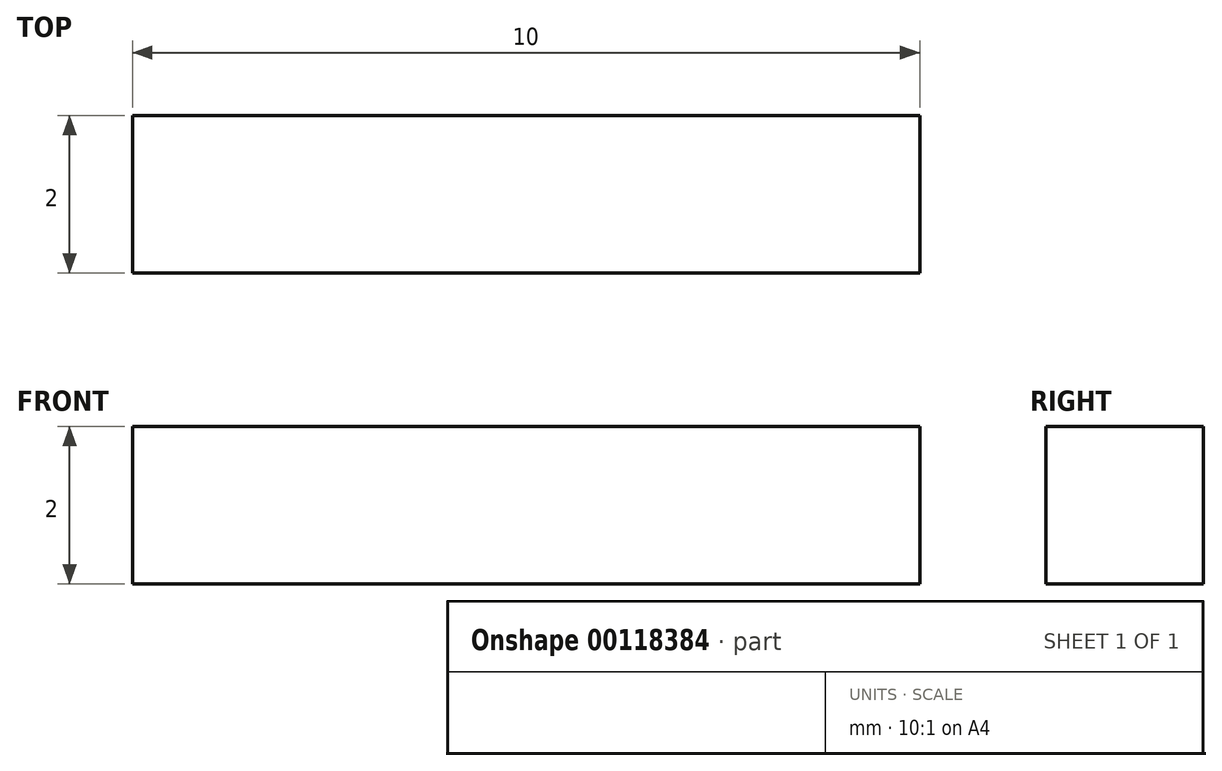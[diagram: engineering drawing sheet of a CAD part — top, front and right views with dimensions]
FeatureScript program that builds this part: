
annotation { "Feature Type Name" : "Feature", "Feature Type Description" : "" }
export const myFeature = defineFeature(function(context is Context, id is Id, definition is map)
    precondition{}
    {
        {
            var Q0;
            Q0=qCreatedBy(makeId("Top.planeOp"),FACE);
            var sketch = newSketch(context, id + "F0", { "sketchPlane" : qUnion([Q0])});
            skLineSegment(sketch, "E0.bottom", {"start": v(5, -1) * mm, "end": v(-5, -1) * mm});
            skLineSegment(sketch, "E0.top", {"start": v(5, 1) * mm, "end": v(-5, 1) * mm});
            skLineSegment(sketch, "E0.left", {"start": v(5, -1) * mm, "end": v(5, 1) * mm});
            skLineSegment(sketch, "E0.right", {"start": v(-5, -1) * mm, "end": v(-5, 1) * mm});
            skPoint(sketch, "E0.middle", {"position": v(0, 0) * mm});
            skSolve(sketch);
        }
        {
            var Q0;
            Q0 = qSketchRegion(id + "F0", true);
            extrude(context, id + "F1", {"entities" : qUnion([Q0]), "depth" : 2 * mm});
        }
    });
